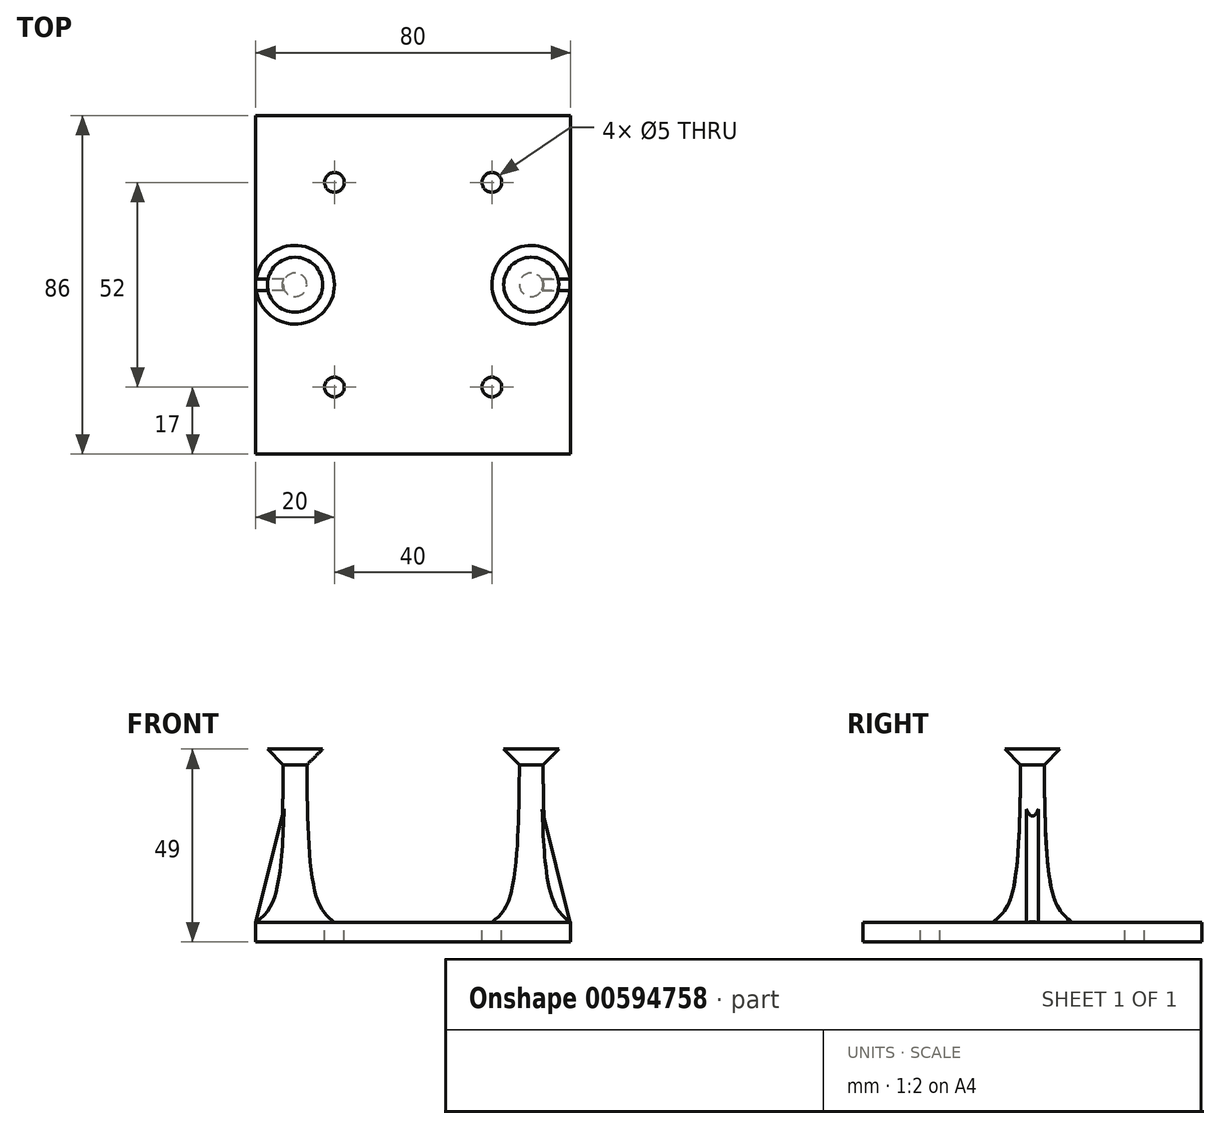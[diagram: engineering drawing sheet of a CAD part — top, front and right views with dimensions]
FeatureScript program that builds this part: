
annotation { "Feature Type Name" : "Feature", "Feature Type Description" : "" }
export const myFeature = defineFeature(function(context is Context, id is Id, definition is map)
    precondition{}
    {
        {
            var Q0;
            Q0=qCreatedBy(makeId("Top.planeOp"),FACE);
            var sketch = newSketch(context, id + "F0", { "sketchPlane" : qUnion([Q0])});
            skLineSegment(sketch, "E0.bottom", {"start": v(40, 43) * mm, "end": v(-40, 43) * mm});
            skLineSegment(sketch, "E0.top", {"start": v(40, -43) * mm, "end": v(-40, -43) * mm});
            skLineSegment(sketch, "E0.left", {"start": v(40, 43) * mm, "end": v(40, -43) * mm});
            skLineSegment(sketch, "E0.right", {"start": v(-40, 43) * mm, "end": v(-40, -43) * mm});
            skPoint(sketch, "E0.middle", {"position": v(0, 0) * mm});
            skLineSegment(sketch, "E1", {"start": v(-40, 26) * mm, "end": v(40, 26) * mm});
            skLineSegment(sketch, "E2", {"start": v(-40, -26) * mm, "end": v(40, -26) * mm});
            skPoint(sketch, "E3", {"position": v(0, 26) * mm});
            skPoint(sketch, "E4", {"position": v(0, -26) * mm});
            skPoint(sketch, "E5", {"position": v(-20, 26) * mm});
            skPoint(sketch, "E6", {"position": v(-20, -26) * mm});
            skPoint(sketch, "E7", {"position": v(20, -26) * mm});
            skPoint(sketch, "E8", {"position": v(20, 26) * mm});
            skPoint(sketch, "E9", {"position": v(-30, 0) * mm});
            skPoint(sketch, "E10", {"position": v(30, 0) * mm});
            skSolve(sketch);
        }
        {
            var Q0;
            Q0=qCreatedBy(makeId("Front.planeOp"),FACE);
            var sketch = newSketch(context, id + "F1", { "sketchPlane" : qUnion([Q0])});
            skPoint(sketch, "E11", {"position": v(-30, 0) * mm});
            skPoint(sketch, "E12", {"position": v(-30, 40) * mm});
            skLineSegment(sketch, "E13", {"start": v(-27, 40) * mm, "end": v(-30, 40) * mm});
            skPoint(sketch, "E14", {"position": v(-20, 0) * mm});
            skPoint(sketch, "E15", {"position": v(20, 0) * mm});
            skPoint(sketch, "E16", {"position": v(30, 0) * mm});
            skLineSegment(sketch, "E17", {"start": v(-30, 40) * mm, "end": v(-30, 0) * mm});
            skLineSegment(sketch, "E18", {"start": v(30, 40) * mm, "end": v(30, 0) * mm});
            skPoint(sketch, "E19", {"position": v(27, 40) * mm});
            skLineSegment(sketch, "E20", {"start": v(27, 40) * mm, "end": v(30, 40) * mm});
            skFitSpline(sketch, "E21", {"points": [v(-20, 0) * mm, v(-24.2, 5.37) * mm, v(-27, 40) * mm], "startDerivative": vector(-15.19, 12.5) * mm, "endDerivative": vector(-0.68, 61.23) * mm});
            skPoint(sketch, "E22", {"position": v(-24.2, 0) * mm});
            skPoint(sketch, "E23", {"position": v(24.2, 0) * mm});
            skPoint(sketch, "E24", {"position": v(24.2, 5.37) * mm});
            skFitSpline(sketch, "E25", {"points": [v(20, 0) * mm, v(24.2, 5.37) * mm, v(27, 40) * mm], "startDerivative": vector(15.19, 12.5) * mm, "endDerivative": vector(0.68, 61.23) * mm});
            skLineSegment(sketch, "E26", {"start": v(-20, 0) * mm, "end": v(-30, 0) * mm});
            skLineSegment(sketch, "E27", {"start": v(20, 0) * mm, "end": v(30, 0) * mm});
            skPoint(sketch, "E28", {"position": v(-40, 0) * mm});
            skPoint(sketch, "E29", {"position": v(39.9, 0) * mm});
            skLineSegment(sketch, "E30", {"start": v(-30, 0) * mm, "end": v(-40, 0) * mm});
            skLineSegment(sketch, "E31", {"start": v(30, 0) * mm, "end": v(39.9, 0) * mm});
            skLineSegment(sketch, "E32", {"start": v(-30, 40) * mm, "end": v(-40, 0) * mm});
            skLineSegment(sketch, "E33", {"start": v(30, 40) * mm, "end": v(39.9, 0) * mm});
            skLineSegment(sketch, "E34", {"start": v(-30, 44) * mm, "end": v(-30, 40) * mm});
            skLineSegment(sketch, "E35", {"start": v(-30, 44) * mm, "end": v(-23, 44) * mm});
            skLineSegment(sketch, "E36", {"start": v(30, 44) * mm, "end": v(23, 44) * mm});
            skLineSegment(sketch, "E37", {"start": v(30, 40) * mm, "end": v(30, 44) * mm});
            skLineSegment(sketch, "E38", {"start": v(-27, 40) * mm, "end": v(-23, 44) * mm});
            skLineSegment(sketch, "E39", {"start": v(27, 40) * mm, "end": v(23, 44) * mm});
            skSolve(sketch);
        }
        {
            var Q0;
            Q0=qCreatedBy(makeId("Right.planeOp"),FACE);
            var sketch = newSketch(context, id + "F2", { "sketchPlane" : qUnion([Q0])});
            skPoint(sketch, "E40", {"position": v(23.28, 0) * mm});
            skPoint(sketch, "E41", {"position": v(23.28, 40) * mm});
            skSolve(sketch);
        }
        {
            var Q0;
            Q0=makeQuery(id+"F1.imprint","IMPRINT",FACE,{"disambiguationData":[TD([[makeQuery(id+"F1.imprint","IMPRINT",EDGE,{"derivedFrom":sQuery(id+"F1.wireOp",EDGE,"E13")}),1.0]])]});
            var Q1;
            Q1=makeQuery(id+"F1.imprint","IMPRINT",FACE,{"disambiguationData":[TD([[makeQuery(id+"F1.imprint","IMPRINT",EDGE,{"derivedFrom":sQuery(id+"F1.wireOp",EDGE,"E13")}),-1.0]])]});
            var Q2;
            Q2=sQuery(id+"F1.wireOp",EDGE,"E17");
            revolve(context, id + "F3", {"entities" : qUnion([Q0, Q1]), "axis" : qUnion([Q2]), "revolveType" : RevolveType.FULL});
        }
        {
            var Q0;
            Q0=makeQuery(id+"F1.imprint","IMPRINT",FACE,{"disambiguationData":[TD([[makeQuery(id+"F1.imprint","IMPRINT",EDGE,{"derivedFrom":sQuery(id+"F1.wireOp",EDGE,"E18")}),-1.0]])]});
            var Q1;
            Q1=makeQuery(id+"F1.imprint","IMPRINT",FACE,{"disambiguationData":[TD([[makeQuery(id+"F1.imprint","IMPRINT",EDGE,{"derivedFrom":sQuery(id+"F1.wireOp",EDGE,"E20")}),1.0]])]});
            var Q2;
            Q2=sQuery(id+"F1.wireOp",EDGE,"E18");
            revolve(context, id + "F4", {"entities" : qUnion([Q0, Q1]), "axis" : qUnion([Q2]), "revolveType" : RevolveType.FULL});
        }
        {
            var Q0;
            {var subQ0=sQuery(id+"F0.wireOp",EDGE,"E0.top");Q0=makeQuery(id+"F0.imprint","IMPRINT",FACE,{"disambiguationData":[TD([[makeQuery(id+"F0.imprint","IMPRINT",EDGE,{"derivedFrom":subQ0}),-1.0]])]});}
            var Q1;
            {var subQ0=sQuery(id+"F0.wireOp",EDGE,"E1");Q1=makeQuery(id+"F0.imprint","IMPRINT",FACE,{"disambiguationData":[TD([[makeQuery(id+"F0.imprint","IMPRINT",EDGE,{"derivedFrom":subQ0}),-1.0]])]});}
            var Q2;
            {var subQ0=sQuery(id+"F0.wireOp",EDGE,"E0.bottom");Q2=makeQuery(id+"F0.imprint","IMPRINT",FACE,{"disambiguationData":[TD([[makeQuery(id+"F0.imprint","IMPRINT",EDGE,{"derivedFrom":subQ0}),1.0]])]});}
            extrude(context, id + "F5", {"entities" : qUnion([Q0, Q1, Q2]), "oppositeDirection" : true, "depth" : 5 * mm, "offsetDistance" : 25 * mm});
        }
        {
            var Q0;
            Q0=sQuery(id+"F0.wireOp",VERTEX,"E6");
            var Q1;
            Q1=sQuery(id+"F0.wireOp",VERTEX,"E5");
            var Q2;
            Q2=sQuery(id+"F0.wireOp",VERTEX,"E8");
            var Q3;
            Q3=sQuery(id+"F0.wireOp",VERTEX,"E7");
            var Q4;
            Q4=makeQuery(id+"F5.opExtrude","SWEPT_BODY",BODY,{"disambiguationData":[OSD([sQuery(id+"F0.wireOp",EDGE,"E0.bottom"),sQuery(id+"F0.wireOp",EDGE,"E0.top"),sQuery(id+"F0.wireOp",EDGE,"E0.left"),sQuery(id+"F0.wireOp",EDGE,"E0.right")])]});
            hole(context, id + "F6", {"style" : HoleStyle.SIMPLE, "endStyle" : HoleEndStyle.THROUGH, "holeDiameter" : 5 * mm, "majorDiameter" : 5 * mm, "isTappedThrough" : true, "tappedDepth" : 12 * mm, "tapClearance" : 3, "locations" : qUnion([Q0, Q1, Q2, Q3]), "scope" : qUnion([Q4])});
        }
        {
            var Q0;
            Q0=makeQuery(id+"F1.imprint","IMPRINT",FACE,{"disambiguationData":[TD([[makeQuery(id+"F1.imprint","IMPRINT",EDGE,{"derivedFrom":sQuery(id+"F1.wireOp",EDGE,"E17")}),-1.0]])]});
            extrude(context, id + "F7", {"entities" : qUnion([Q0]), "operationType" : NewBodyOperationType.ADD, "endBound" : BoundingType.SYMMETRIC, "depth" : 3 * mm, "offsetDistance" : 25 * mm});
        }
        {
            var Q0;
            Q0=makeQuery(id+"F1.imprint","IMPRINT",FACE,{"disambiguationData":[TD([[makeQuery(id+"F1.imprint","IMPRINT",EDGE,{"derivedFrom":sQuery(id+"F1.wireOp",EDGE,"E18")}),1.0]])]});
            extrude(context, id + "F8", {"entities" : qUnion([Q0]), "operationType" : NewBodyOperationType.ADD, "endBound" : BoundingType.SYMMETRIC, "depth" : 3 * mm, "offsetDistance" : 25 * mm});
        }
    });
